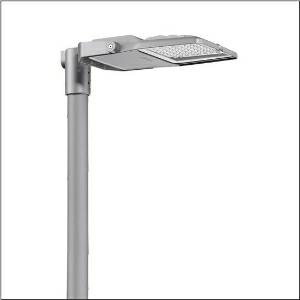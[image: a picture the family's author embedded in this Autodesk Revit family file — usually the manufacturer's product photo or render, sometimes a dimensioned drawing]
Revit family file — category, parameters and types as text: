
# Revit family: floodlight_fl_21_iq_mini___pl61_5xa7771b2c3a_a4a3
name_source: partatom
category: Lighting Fixtures
units: mm (PartAtom-declared; Revit-internal decimal feet)

## family parameters
Cut with Voids When Loaded = No
Host = Face
Light Source = No
Part Type = Normal
Room Calculation Point = No
Round Connector Dimension = Use Diameter
Shared = No

## types (1)
- --- (1 x LED, 6120 lm, 45.5 W, 3000K)
    Apparent Load = 46 VA
    CIE Flux Codes = 33 65 98 100 100
    Color Rendering = 70
    Color Temperature = 3000K
    Default Elevation = 1800 mm
    Description = Floodlight FL 21 iQ mini, floodlight, primary light control with lens, of PMMA, primary optical cover: protective disc, of toughened safety glass, transparent, light distribution: PL61, light emission: direct distribution, installation type: surface-mounted, LED, High Power LED, rated luminous flux: 6.120lm, luminous efficacy: 135lm/W, light colour: 730, colour temperature: 3000K, control gear: iQ Comfort/DALI, control: Auto-Match, Temp-Guard, Lumen-Switch, Night-Set, Smart-Wire, Light-Fading, Desk-Remote (wireless, voltage-free reading and setting of iQ features in the workshop via application-optimized NFC function/RFID function), optimised constant luminous flux control (CLO 2.0), with terminal, 6-pole, mains connection: 220..240V, AC, 50/60Hz, start of lifetime: 46W, end of service life: 48W, reduction: 22W, luminaire housing, of diecast aluminium, powder-coated, Siteco® metallic grey (DB 702S), corrosivity category C5 mid according to DIN EN ISO 12944, suitable for swimming pools, chlorine-resistant, sealing non-destructively replaceable, please order mast flange separately, mast bracket, of steel, galvanised, powder-coated, Siteco® metallic grey (DB 702S), protection rating (complete): IP66, insulation class (complete): insulation class II (safety insulation), certification: CE, ENEC, VDE, protection symbol: D, impact resistance: IK08, permissible operating ambient temperature: -40..+40°C, permissible operating ambient temperature for outdoor applications: -40..+50°C, standard: DIN EN 12944, LABS conformity tested according to VDMA 24364:2018-05, packaging unit: 1 piece

Light Distribution: PL61
    Height = 70 mm
    Lamp = 1 x LED
    Lamp Light Flux = 6120 lm
    Lamp Power = 45.5 W
    Lamp count = 1
    Length = 485 mm
    Luminous efficacy = 135 lm/W
    Manufacturer = Siteco
    ModVariant = No
    Model = 5XA7771B2C3A
    Number of Poles = 1
    OnlyDefault = Yes
    Power Factor = 1
    Product Name = Floodlight FL 21 iQ mini | PL61
    Product group = floodlight | pylon annexe
    ProductGroupID = 6201
    Protection Class = Protection class II
    Protection Degree = IP 66
    RLX_Detail_Level = 1
    RLX_Emergency_Light_Flux = 0 lm
    RLX_Emergency_Type = 0
    RLX_Emergency_Type_DB = No
    RlxData = <blob elided: 101405 chars, md5=6f2e9e75>
    Socket = socket
    Standby Power = 0 W
    System Light Flux = 6120 lm
    System Power = 46 W
    Type Comments = factory setting: luminous flux: 100 % | dim-lin: 254 | 463 mA
    Type Image = l_1007125.jpg
    URL = http://relux.com
    VarID = @adj_195309
    Voltage = 0 V
    Weight = 0.00 kg
    Width = 337 mm

## geometry (parser evidence)
native form markers: Blend x4, Sweep x12
no freeform markers — native parametric forms only
